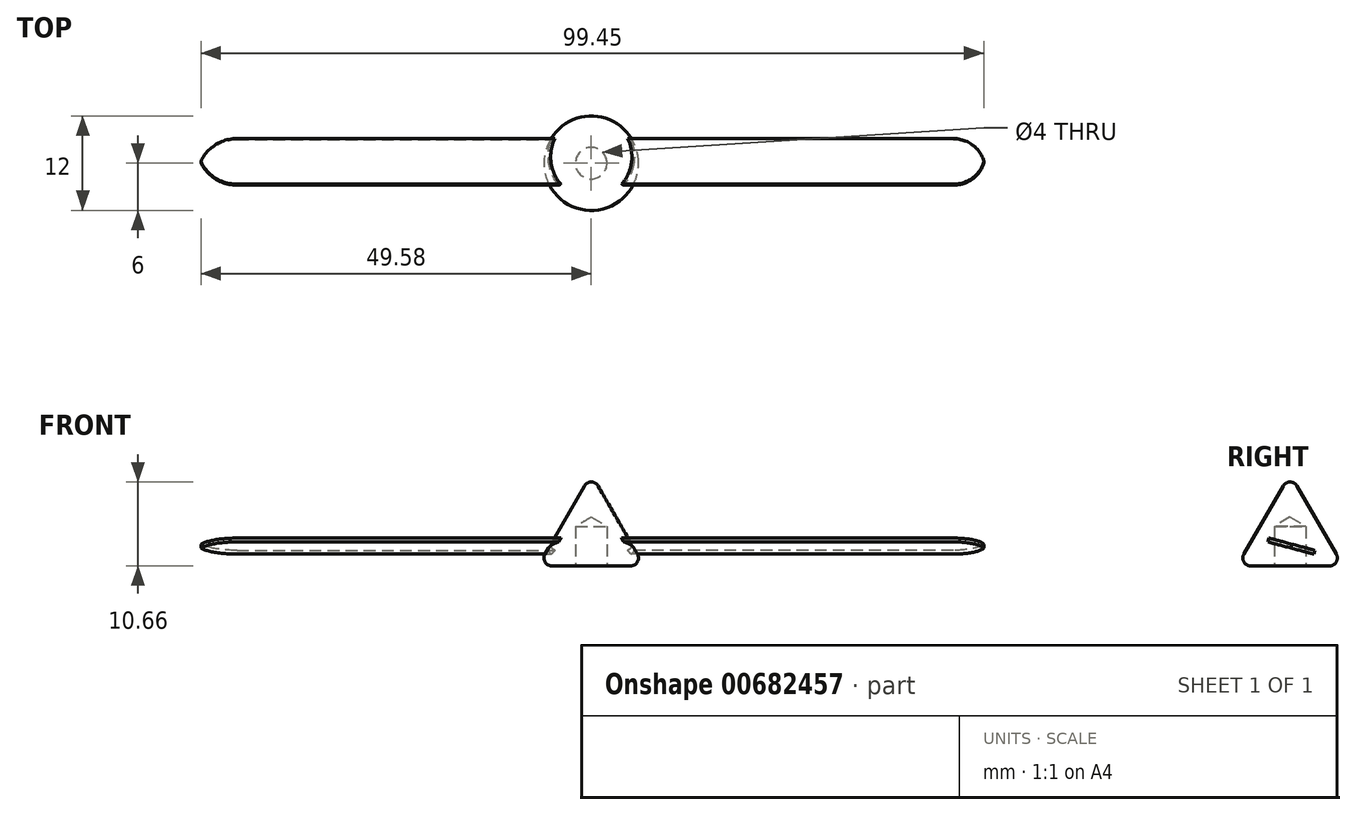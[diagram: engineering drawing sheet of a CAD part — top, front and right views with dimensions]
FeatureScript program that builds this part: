
annotation { "Feature Type Name" : "Feature", "Feature Type Description" : "" }
export const myFeature = defineFeature(function(context is Context, id is Id, definition is map)
    precondition{}
    {
        {
            var Q0;
            Q0=qCreatedBy(makeId("Right.planeOp"),FACE);
            var sketch = newSketch(context, id + "F0", { "sketchPlane" : qUnion([Q0])});
            skLineSegment(sketch, "E0", {"start": v(0.87, 10.16) * mm, "end": v(5.87, 1.5) * mm});
            skLineSegment(sketch, "E1", {"start": v(5, 0) * mm, "end": v(0, 0) * mm});
            skPoint(sketch, "E2.visualSharp", {"position": v(0, 0) * mm});
            skPoint(sketch, "E3.visualSharp", {"position": v(6.73, 0) * mm});
            skArc(sketch, "E3.filletArc", {"start": v(5, 0) * mm, "mid": v(5.87, 0.5) * mm, "end": v(5.87, 1.5) * mm});
            skArc(sketch, "E4.filletArc", {"start": v(0.87, 10.16) * mm, "mid": v(0.5, 10.53) * mm, "end": v(0, 10.66) * mm});
            skPoint(sketch, "E5.startSnap0", {"position": v(0, 10.66) * mm});
            skLineSegment(sketch, "E6", {"start": v(0, 18.03) * mm, "end": v(0, -13.66) * mm, "construction": true});
            skLineSegment(sketch, "E7", {"start": v(0, 10.66) * mm, "end": v(0, 0) * mm});
            skSolve(sketch);
        }
        {
            var Q0;
            Q0 = qSketchRegion(id + "F0", true);
            var Q1;
            Q1=sQuery(id+"F0.wireOp",EDGE,"E6");
            revolve(context, id + "F1", {"entities" : qUnion([Q0]), "axis" : qUnion([Q1]), "revolveType" : RevolveType.FULL});
        }
        {
            var Q0;
            Q0=qCreatedBy(makeId("Right.planeOp"),FACE);
            var sketch = newSketch(context, id + "F2", { "sketchPlane" : qUnion([Q0])});
            skLineSegment(sketch, "E8", {"start": v(-2.67, 3.54) * mm, "end": v(3.13, 1.98) * mm});
            skLineSegment(sketch, "E9", {"start": v(3.13, 1.98) * mm, "end": v(3, 1.5) * mm});
            skLineSegment(sketch, "E10", {"start": v(3, 1.5) * mm, "end": v(-2.8, 3.05) * mm});
            skLineSegment(sketch, "E11", {"start": v(-2.8, 3.05) * mm, "end": v(-2.67, 3.54) * mm});
            skSolve(sketch);
        }
        {
            var Q0;
            Q0 = qSketchRegion(id + "F2", true);
            extrude(context, id + "F3", {"entities" : qUnion([Q0]), "operationType" : NewBodyOperationType.ADD, "depth" : 50 * mm, "offsetDistance" : 25 * mm});
        }
        {
            var Q0;
            Q0=makeQuery(id+"F3.opExtrude","CAP_EDGE",EDGE,{"disambiguationData":[OSD([sQuery(id+"F2.wireOp",EDGE,"E11")])],"isStart":false});
            var Q1;
            Q1=makeQuery(id+"F3.opExtrude","CAP_EDGE",EDGE,{"disambiguationData":[OSD([sQuery(id+"F2.wireOp",EDGE,"E9")])],"isStart":false});
            fillet(context, id + "F4", {"entities" : qUnion([Q0, Q1]), "radius" : 4 * mm, "tangentPropagation" : true, "allowEdgeOverflow" : false});
        }
        {
            var Q0;
            Q0=qCreatedBy(makeId("Right.planeOp"),FACE);
            var sketch = newSketch(context, id + "F5", { "sketchPlane" : qUnion([Q0])});
            skLineSegment(sketch, "E12", {"start": v(3.13, 1.98) * mm, "end": v(-2.67, 3.54) * mm});
            skLineSegment(sketch, "E13", {"start": v(-2.67, 3.54) * mm, "end": v(-2.8, 3.05) * mm});
            skLineSegment(sketch, "E14", {"start": v(-2.8, 3.05) * mm, "end": v(3, 1.5) * mm});
            skLineSegment(sketch, "E15", {"start": v(3, 1.5) * mm, "end": v(3.13, 1.98) * mm});
            skSolve(sketch);
        }
        {
            var Q0;
            Q0 = qSketchRegion(id + "F5", true);
            extrude(context, id + "F6", {"entities" : qUnion([Q0]), "operationType" : NewBodyOperationType.ADD, "oppositeDirection" : true, "depth" : 50 * mm, "offsetDistance" : 25 * mm});
        }
        {
            var Q0;
            Q0=makeQuery(id+"F6.opExtrude","CAP_EDGE",EDGE,{"disambiguationData":[OSD([sQuery(id+"F5.wireOp",EDGE,"E15")])],"isStart":false});
            var Q1;
            Q1=makeQuery(id+"F6.opExtrude","CAP_EDGE",EDGE,{"disambiguationData":[OSD([sQuery(id+"F5.wireOp",EDGE,"E13")])],"isStart":false});
            fillet(context, id + "F7", {"entities" : qUnion([Q0, Q1]), "radius" : 5 * mm, "tangentPropagation" : true, "allowEdgeOverflow" : false});
        }
        {
            var Q0;
            Q0=makeQuery(id+"F1.opRevolve","SWEPT_FACE",FACE,{"disambiguationData":[OSD([sQuery(id+"F0.wireOp",EDGE,"E1")])]});
            var sketch = newSketch(context, id + "F8", { "sketchPlane" : qUnion([Q0])});
            skCircle(sketch, "E16", {"center": v(0, 0) * mm, "radius": 1 * mm});
            skSolve(sketch);
        }
        {
            var Q0;
            Q0=sQuery(id+"F8.wireOp",VERTEX,"E16.center");
            var Q1;
            Q1=makeQuery(id+"F1.opRevolve","SWEPT_BODY",BODY,{"disambiguationData":[OSD([sQuery(id+"F0.wireOp",EDGE,"E0"),sQuery(id+"F0.wireOp",EDGE,"E1"),sQuery(id+"F0.wireOp",EDGE,"E3.filletArc"),sQuery(id+"F0.wireOp",EDGE,"E4.filletArc"),sQuery(id+"F0.wireOp",EDGE,"E7")])]});
            hole(context, id + "F9", {"style" : HoleStyle.SIMPLE, "endStyle" : HoleEndStyle.BLIND, "holeDiameter" : 4 * mm, "majorDiameter" : 3 * mm, "holeDepth" : 5 * mm, "isTappedThrough" : true, "tappedDepth" : 3.5 * mm, "tapClearance" : 3, "locations" : qUnion([Q0]), "scope" : qUnion([Q1])});
        }
    });
